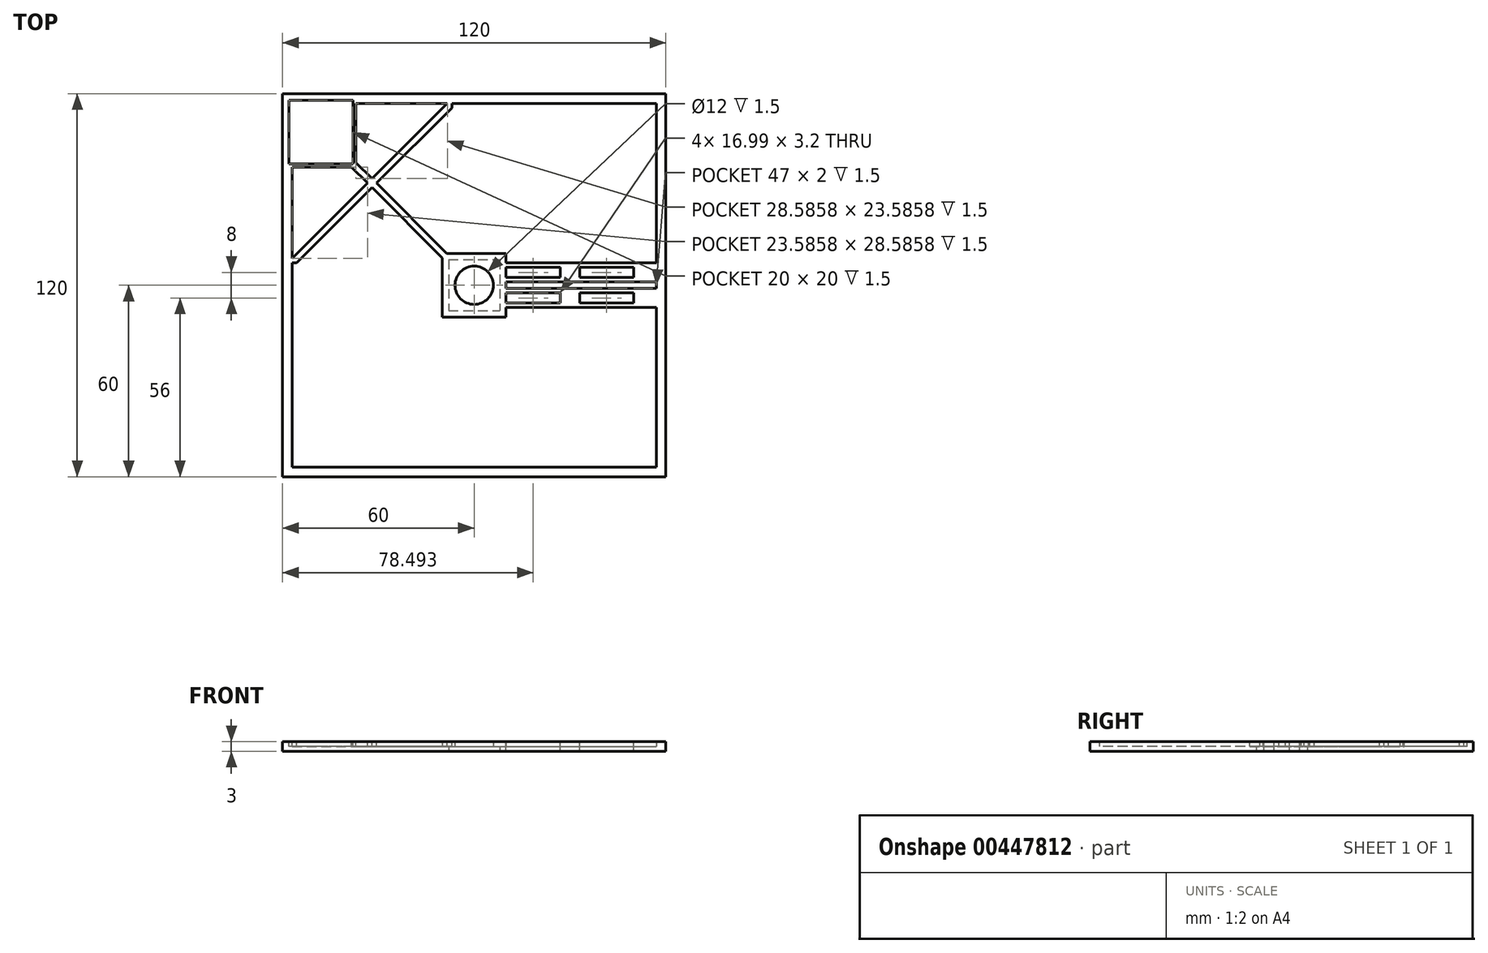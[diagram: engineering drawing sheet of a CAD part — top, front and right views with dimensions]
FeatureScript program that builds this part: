
annotation { "Feature Type Name" : "Feature", "Feature Type Description" : "" }
export const myFeature = defineFeature(function(context is Context, id is Id, definition is map)
    precondition{}
    {
        {
            var Q0;
            Q0=qCreatedBy(makeId("Top.planeOp"),FACE);
            var sketch = newSketch(context, id + "F0", { "sketchPlane" : qUnion([Q0])});
            skLineSegment(sketch, "E0.bottom", {"start": v(-60, 60) * mm, "end": v(60, 60) * mm});
            skLineSegment(sketch, "E0.top", {"start": v(-60, -60) * mm, "end": v(60, -60) * mm});
            skLineSegment(sketch, "E0.left", {"start": v(-60, 60) * mm, "end": v(-60, -60) * mm});
            skLineSegment(sketch, "E0.right", {"start": v(60, 60) * mm, "end": v(60, -60) * mm});
            skPoint(sketch, "E0.middle", {"position": v(0, 0) * mm});
            skSolve(sketch);
        }
        {
            var Q0;
            Q0 = qSketchRegion(id + "F0", true);
            extrude(context, id + "F1", {"entities" : qUnion([Q0]), "depth" : 3 * mm});
        }
        {
            var Q0;
            Q0=makeQuery(id+"F1.opExtrude","CAP_FACE",FACE,{"disambiguationData":[OSD([sQuery(id+"F0.wireOp",EDGE,"E0.bottom"),sQuery(id+"F0.wireOp",EDGE,"E0.top"),sQuery(id+"F0.wireOp",EDGE,"E0.left"),sQuery(id+"F0.wireOp",EDGE,"E0.right")])],"isStart":false});
            var sketch = newSketch(context, id + "F2", { "sketchPlane" : qUnion([Q0])});
            skLineSegment(sketch, "E1.bottom", {"start": v(-57, 57) * mm, "end": v(57, 57) * mm});
            skLineSegment(sketch, "E1.top", {"start": v(-57, -57) * mm, "end": v(57, -57) * mm});
            skLineSegment(sketch, "E1.left", {"start": v(-57, 57) * mm, "end": v(-57, -57) * mm});
            skLineSegment(sketch, "E1.right", {"start": v(57, 57) * mm, "end": v(57, -57) * mm});
            skPoint(sketch, "E1.middle", {"position": v(0, 0) * mm});
            skSolve(sketch);
        }
        {
            var Q0;
            Q0 = qSketchRegion(id + "F2", true);
            extrude(context, id + "F3", {"entities" : qUnion([Q0]), "operationType" : NewBodyOperationType.REMOVE, "oppositeDirection" : true, "depth" : 1.5 * mm});
        }
        {
            var Q0;
            Q0=makeQuery(id+"F3.boolean.opBoolean","COPY",FACE,{"derivedFrom":makeQuery(id+"F3.opExtrude","CAP_FACE",FACE,{"disambiguationData":[OSD([sQuery(id+"F2.wireOp",EDGE,"E1.bottom"),sQuery(id+"F2.wireOp",EDGE,"E1.top"),sQuery(id+"F2.wireOp",EDGE,"E1.left"),sQuery(id+"F2.wireOp",EDGE,"E1.right")])],"isStart":false})});
            var sketch = newSketch(context, id + "F4", { "sketchPlane" : qUnion([Q0])});
            skLineSegment(sketch, "E2", {"start": v(0, 0) * mm, "end": v(57, 0) * mm});
            skSolve(sketch);
        }
        {
            var Q0;
            {var subQ1=makeQuery(id+"F3.boolean.opBoolean","COPY",EDGE,{"derivedFrom":makeQuery(id+"F3.opExtrude","CAP_EDGE",EDGE,{"disambiguationData":[OSD([sQuery(id+"F2.wireOp",EDGE,"E1.bottom")])],"isStart":false})});Q0=makeQuery(id+"F4.imprint","IMPRINT",FACE,{"disambiguationData":[TD([[makeQuery(id+"F4.imprint","IMPRINT",EDGE,{"derivedFrom":subQ1}),-1.0]])]});}
            var sketch = newSketch(context, id + "F5", { "sketchPlane" : qUnion([Q0])});
            skLineSegment(sketch, "E3.bottom", {"start": v(-0.17, -1) * mm, "end": v(57, -1) * mm});
            skLineSegment(sketch, "E3.top", {"start": v(-0.17, -7) * mm, "end": v(57, -7) * mm});
            skLineSegment(sketch, "E3.left", {"start": v(-0.17, -1) * mm, "end": v(-0.17, -7) * mm});
            skLineSegment(sketch, "E3.right", {"start": v(57, -1) * mm, "end": v(57, -7) * mm});
            skLineSegment(sketch, "E4.MirrorCS", {"start": v(-0.17, 1) * mm, "end": v(57, 1) * mm});
            skLineSegment(sketch, "E5.MirrorCS", {"start": v(-0.17, 1) * mm, "end": v(-0.17, 7) * mm});
            skLineSegment(sketch, "E6.MirrorCS", {"start": v(-0.17, 7) * mm, "end": v(57, 7) * mm});
            skLineSegment(sketch, "E7.MirrorCS", {"start": v(57, 1) * mm, "end": v(57, 7) * mm});
            skSolve(sketch);
        }
        {
            var Q0;
            Q0 = qSketchRegion(id + "F5", true);
            extrude(context, id + "F6", {"entities" : qUnion([Q0]), "operationType" : NewBodyOperationType.ADD, "depth" : 1.5 * mm});
        }
        {
            var Q0;
            Q0=qCreatedBy(makeId("Front.planeOp"),FACE);
            var sketch = newSketch(context, id + "F7", { "sketchPlane" : qUnion([Q0])});
            skLineSegment(sketch, "E8", {"start": v(0, 0) * mm, "end": v(0, 23.02) * mm});
            skSolve(sketch);
        }
        {
            var Q0;
            {var subQ0=sQuery(id+"F5.wireOp",EDGE,"E7.MirrorCS");var subQ1=sQuery(id+"F5.wireOp",EDGE,"E6.MirrorCS");var subQ2=sQuery(id+"F5.wireOp",EDGE,"E5.MirrorCS");var subQ3=sQuery(id+"F5.wireOp",EDGE,"E4.MirrorCS");var subQ4=sQuery(id+"F5.wireOp",EDGE,"E3.right");var subQ5=sQuery(id+"F5.wireOp",EDGE,"E3.left");var subQ6=sQuery(id+"F5.wireOp",EDGE,"E3.top");var subQ7=sQuery(id+"F5.wireOp",EDGE,"E3.bottom");Q0=makeQuery(id+"FaZMyGU1LHLxgY4_1.3.F6.boolean.opBoolean","MERGE",FACE,{"derivedFrom":[makeQuery(id+"FaZMyGU1LHLxgY4_1.2.F6.boolean.opBoolean","MERGE",FACE,{"derivedFrom":[makeQuery(id+"FaZMyGU1LHLxgY4_1.1.F6.boolean.opBoolean","MERGE",FACE,{"derivedFrom":[makeQuery(id+"F6.boolean.opBoolean","MERGE",FACE,{"derivedFrom":[makeQuery(id+"F1.opExtrude","CAP_FACE",FACE,{"disambiguationData":[OSD([sQuery(id+"F0.wireOp",EDGE,"E0.bottom"),sQuery(id+"F0.wireOp",EDGE,"E0.top"),sQuery(id+"F0.wireOp",EDGE,"E0.left"),sQuery(id+"F0.wireOp",EDGE,"E0.right")])],"isStart":false}),makeQuery(id+"F6.opExtrude","CAP_FACE",FACE,{"disambiguationData":[OSD([subQ7,subQ6,subQ5,subQ4])],"isStart":false}),makeQuery(id+"F6.opExtrude","CAP_FACE",FACE,{"disambiguationData":[OSD([subQ3,subQ2,subQ1,subQ0])],"isStart":false})]}),makeQuery(id+"FaZMyGU1LHLxgY4_1.1.F6.opExtrude","CAP_FACE",FACE,{"disambiguationData":[OSD([subQ7,subQ6,subQ5,subQ4])],"isStart":false}),makeQuery(id+"FaZMyGU1LHLxgY4_1.1.F6.opExtrude","CAP_FACE",FACE,{"disambiguationData":[OSD([subQ3,subQ2,subQ1,subQ0])],"isStart":false})]}),makeQuery(id+"FaZMyGU1LHLxgY4_1.2.F6.opExtrude","CAP_FACE",FACE,{"disambiguationData":[OSD([subQ7,subQ6,subQ5,subQ4])],"isStart":false}),makeQuery(id+"FaZMyGU1LHLxgY4_1.2.F6.opExtrude","CAP_FACE",FACE,{"disambiguationData":[OSD([subQ3,subQ2,subQ1,subQ0])],"isStart":false})]}),makeQuery(id+"FaZMyGU1LHLxgY4_1.3.F6.opExtrude","CAP_FACE",FACE,{"disambiguationData":[OSD([subQ7,subQ6,subQ5,subQ4])],"isStart":false}),makeQuery(id+"FaZMyGU1LHLxgY4_1.3.F6.opExtrude","CAP_FACE",FACE,{"disambiguationData":[OSD([subQ3,subQ2,subQ1,subQ0])],"isStart":false})]});}
            var sketch = newSketch(context, id + "F8", { "sketchPlane" : qUnion([Q0])});
            skLineSegment(sketch, "E9.bottom", {"start": v(10, -5.6) * mm, "end": v(26.99, -5.6) * mm});
            skLineSegment(sketch, "E9.top", {"start": v(10, -2.4) * mm, "end": v(26.99, -2.4) * mm});
            skLineSegment(sketch, "E9.left", {"start": v(10, -5.6) * mm, "end": v(10, -2.4) * mm});
            skLineSegment(sketch, "E9.right", {"start": v(26.99, -5.6) * mm, "end": v(26.99, -2.4) * mm});
            skLineSegment(sketch, "E10.bottom", {"start": v(33, -5.6) * mm, "end": v(49.99, -5.6) * mm});
            skLineSegment(sketch, "E10.top", {"start": v(33, -2.4) * mm, "end": v(49.99, -2.4) * mm});
            skLineSegment(sketch, "E10.left", {"start": v(33, -5.6) * mm, "end": v(33, -2.4) * mm});
            skLineSegment(sketch, "E10.right", {"start": v(49.99, -5.6) * mm, "end": v(49.99, -2.4) * mm});
            skLineSegment(sketch, "E11.MirrorCS", {"start": v(49.99, 5.6) * mm, "end": v(49.99, 2.4) * mm});
            skLineSegment(sketch, "E12.MirrorCS", {"start": v(26.99, 5.6) * mm, "end": v(26.99, 2.4) * mm});
            skLineSegment(sketch, "E13.MirrorCS", {"start": v(10, 5.6) * mm, "end": v(10, 2.4) * mm});
            skLineSegment(sketch, "E14.MirrorCS", {"start": v(10, 2.4) * mm, "end": v(26.99, 2.4) * mm});
            skLineSegment(sketch, "E15.MirrorCS", {"start": v(10, 5.6) * mm, "end": v(26.99, 5.6) * mm});
            skLineSegment(sketch, "E16.MirrorCS", {"start": v(33, 5.6) * mm, "end": v(49.99, 5.6) * mm});
            skLineSegment(sketch, "E17.MirrorCS", {"start": v(33, 2.4) * mm, "end": v(49.99, 2.4) * mm});
            skLineSegment(sketch, "E18.MirrorCS", {"start": v(33, 5.6) * mm, "end": v(33, 2.4) * mm});
            skSolve(sketch);
        }
        {
            var Q0;
            Q0 = qSketchRegion(id + "F8", true);
            extrude(context, id + "F9", {"entities" : qUnion([Q0]), "operationType" : NewBodyOperationType.REMOVE, "oppositeDirection" : true, "depth" : 3 * mm});
        }
        {
            var Q0;
            {var subQ1=makeQuery(id+"F3.boolean.opBoolean","COPY",EDGE,{"derivedFrom":makeQuery(id+"F3.opExtrude","CAP_EDGE",EDGE,{"disambiguationData":[OSD([sQuery(id+"F2.wireOp",EDGE,"E1.bottom")])],"isStart":false})});Q0=makeQuery(id+"F4.imprint","IMPRINT",FACE,{"disambiguationData":[TD([[makeQuery(id+"F4.imprint","IMPRINT",EDGE,{"derivedFrom":subQ1}),-1.0]])]});}
            var sketch = newSketch(context, id + "F10", { "sketchPlane" : qUnion([Q0])});
            skLineSegment(sketch, "E19.bottom", {"start": v(-59, 59) * mm, "end": v(-37, 59) * mm});
            skLineSegment(sketch, "E19.top", {"start": v(-59, 37) * mm, "end": v(-37, 37) * mm});
            skLineSegment(sketch, "E19.left", {"start": v(-59, 59) * mm, "end": v(-59, 37) * mm});
            skLineSegment(sketch, "E19.right", {"start": v(-37, 59) * mm, "end": v(-37, 37) * mm});
            skPoint(sketch, "E19.middle", {"position": v(-48, 48) * mm});
            skLineSegment(sketch, "E20.bottom", {"start": v(-40.5, 55.5) * mm, "end": v(-55.5, 55.5) * mm});
            skLineSegment(sketch, "E20.top", {"start": v(-40.5, 40.5) * mm, "end": v(-55.5, 40.5) * mm});
            skLineSegment(sketch, "E20.left", {"start": v(-40.5, 55.5) * mm, "end": v(-40.5, 40.5) * mm});
            skLineSegment(sketch, "E20.right", {"start": v(-55.5, 55.5) * mm, "end": v(-55.5, 40.5) * mm});
            skSolve(sketch);
        }
        {
            var Q0;
            Q0 = qSketchRegion(id + "F10", true);
            extrude(context, id + "F11", {"entities" : qUnion([Q0]), "operationType" : NewBodyOperationType.ADD, "depth" : 1.5 * mm});
        }
        {
            var Q0;
            {var subQ0=sQuery(id+"F10.wireOp",EDGE,"E20.right");var subQ1=sQuery(id+"F10.wireOp",EDGE,"E20.left");var subQ2=sQuery(id+"F10.wireOp",EDGE,"E20.top");var subQ3=sQuery(id+"F10.wireOp",EDGE,"E20.bottom");var subQ4=sQuery(id+"F10.wireOp",EDGE,"E19.right");var subQ5=sQuery(id+"F10.wireOp",EDGE,"E19.left");var subQ6=sQuery(id+"F10.wireOp",EDGE,"E19.top");var subQ7=sQuery(id+"F10.wireOp",EDGE,"E19.bottom");var subQ8=sQuery(id+"F5.wireOp",EDGE,"E7.MirrorCS");var subQ9=sQuery(id+"F5.wireOp",EDGE,"E6.MirrorCS");var subQ10=sQuery(id+"F5.wireOp",EDGE,"E5.MirrorCS");var subQ11=sQuery(id+"F5.wireOp",EDGE,"E4.MirrorCS");var subQ12=sQuery(id+"F5.wireOp",EDGE,"E3.right");var subQ13=sQuery(id+"F5.wireOp",EDGE,"E3.left");var subQ14=sQuery(id+"F5.wireOp",EDGE,"E3.top");var subQ15=sQuery(id+"F5.wireOp",EDGE,"E3.bottom");Q0=makeQuery(id+"F5DrHdDq57b8UHH_1.3.F11.boolean.opBoolean","MERGE",FACE,{"derivedFrom":[makeQuery(id+"F5DrHdDq57b8UHH_1.2.F11.boolean.opBoolean","MERGE",FACE,{"derivedFrom":[makeQuery(id+"F5DrHdDq57b8UHH_1.1.F11.boolean.opBoolean","MERGE",FACE,{"derivedFrom":[makeQuery(id+"F11.boolean.opBoolean","MERGE",FACE,{"derivedFrom":[makeQuery(id+"FaZMyGU1LHLxgY4_1.3.F6.boolean.opBoolean","MERGE",FACE,{"derivedFrom":[makeQuery(id+"FaZMyGU1LHLxgY4_1.2.F6.boolean.opBoolean","MERGE",FACE,{"derivedFrom":[makeQuery(id+"FaZMyGU1LHLxgY4_1.1.F6.boolean.opBoolean","MERGE",FACE,{"derivedFrom":[makeQuery(id+"F6.boolean.opBoolean","MERGE",FACE,{"derivedFrom":[makeQuery(id+"F1.opExtrude","CAP_FACE",FACE,{"disambiguationData":[OSD([sQuery(id+"F0.wireOp",EDGE,"E0.bottom"),sQuery(id+"F0.wireOp",EDGE,"E0.top"),sQuery(id+"F0.wireOp",EDGE,"E0.left"),sQuery(id+"F0.wireOp",EDGE,"E0.right")])],"isStart":false}),makeQuery(id+"F6.opExtrude","CAP_FACE",FACE,{"disambiguationData":[OSD([subQ15,subQ14,subQ13,subQ12])],"isStart":false}),makeQuery(id+"F6.opExtrude","CAP_FACE",FACE,{"disambiguationData":[OSD([subQ11,subQ10,subQ9,subQ8])],"isStart":false})]}),makeQuery(id+"FaZMyGU1LHLxgY4_1.1.F6.opExtrude","CAP_FACE",FACE,{"disambiguationData":[OSD([subQ15,subQ14,subQ13,subQ12])],"isStart":false}),makeQuery(id+"FaZMyGU1LHLxgY4_1.1.F6.opExtrude","CAP_FACE",FACE,{"disambiguationData":[OSD([subQ11,subQ10,subQ9,subQ8])],"isStart":false})]}),makeQuery(id+"FaZMyGU1LHLxgY4_1.2.F6.opExtrude","CAP_FACE",FACE,{"disambiguationData":[OSD([subQ15,subQ14,subQ13,subQ12])],"isStart":false}),makeQuery(id+"FaZMyGU1LHLxgY4_1.2.F6.opExtrude","CAP_FACE",FACE,{"disambiguationData":[OSD([subQ11,subQ10,subQ9,subQ8])],"isStart":false})]}),makeQuery(id+"FaZMyGU1LHLxgY4_1.3.F6.opExtrude","CAP_FACE",FACE,{"disambiguationData":[OSD([subQ15,subQ14,subQ13,subQ12])],"isStart":false}),makeQuery(id+"FaZMyGU1LHLxgY4_1.3.F6.opExtrude","CAP_FACE",FACE,{"disambiguationData":[OSD([subQ11,subQ10,subQ9,subQ8])],"isStart":false})]}),makeQuery(id+"F11.opExtrude","CAP_FACE",FACE,{"disambiguationData":[OSD([subQ7,subQ6,subQ5,subQ4,subQ3,subQ2,subQ1,subQ0])],"isStart":false})]}),makeQuery(id+"F5DrHdDq57b8UHH_1.1.F11.opExtrude","CAP_FACE",FACE,{"disambiguationData":[OSD([subQ7,subQ6,subQ5,subQ4,subQ3,subQ2,subQ1,subQ0])],"isStart":false})]}),makeQuery(id+"F5DrHdDq57b8UHH_1.2.F11.opExtrude","CAP_FACE",FACE,{"disambiguationData":[OSD([subQ7,subQ6,subQ5,subQ4,subQ3,subQ2,subQ1,subQ0])],"isStart":false})]}),makeQuery(id+"F5DrHdDq57b8UHH_1.3.F11.opExtrude","CAP_FACE",FACE,{"disambiguationData":[OSD([subQ7,subQ6,subQ5,subQ4,subQ3,subQ2,subQ1,subQ0])],"isStart":false})]});}
            var sketch = newSketch(context, id + "F12", { "sketchPlane" : qUnion([Q0])});
            skLineSegment(sketch, "E21.bottom", {"start": v(-38, 58) * mm, "end": v(-58, 58) * mm});
            skLineSegment(sketch, "E21.top", {"start": v(-38, 38) * mm, "end": v(-58, 38) * mm});
            skLineSegment(sketch, "E21.left", {"start": v(-38, 58) * mm, "end": v(-38, 38) * mm});
            skLineSegment(sketch, "E21.right", {"start": v(-58, 58) * mm, "end": v(-58, 38) * mm});
            skPoint(sketch, "E21.middle", {"position": v(-48, 48) * mm});
            skLineSegment(sketch, "E22.bottom", {"start": v(-41, 55) * mm, "end": v(-55, 55) * mm});
            skLineSegment(sketch, "E22.top", {"start": v(-41, 41) * mm, "end": v(-55, 41) * mm});
            skLineSegment(sketch, "E22.left", {"start": v(-41, 55) * mm, "end": v(-41, 41) * mm});
            skLineSegment(sketch, "E22.right", {"start": v(-55, 55) * mm, "end": v(-55, 41) * mm});
            skSolve(sketch);
        }
        {
            var Q0;
            Q0 = qSketchRegion(id + "F12", true);
            extrude(context, id + "F13", {"entities" : qUnion([Q0]), "operationType" : NewBodyOperationType.REMOVE, "oppositeDirection" : true, "depth" : 1.5 * mm});
        }
        {
            var Q0;
            {var subQ0=sQuery(id+"F10.wireOp",EDGE,"E19.top");var subQ2=sQuery(id+"F10.wireOp",EDGE,"E19.right");var subQ65=sQuery(id+"F5.wireOp",EDGE,"E3.top");var subQ67=sQuery(id+"F5.wireOp",EDGE,"E4.MirrorCS");var subQ69=sQuery(id+"F5.wireOp",EDGE,"E3.bottom");var subQ74=sQuery(id+"F5.wireOp",EDGE,"E6.MirrorCS");var subQ81=sQuery(id+"F0.wireOp",EDGE,"E0.bottom");var subQ82=makeQuery(id+"F1.opExtrude","SWEPT_FACE",FACE,{"disambiguationData":[OSD([subQ81])]});var subQ86=sQuery(id+"F0.wireOp",EDGE,"E0.left");var subQ91=sQuery(id+"F0.wireOp",EDGE,"E0.top");var subQ110=sQuery(id+"F0.wireOp",EDGE,"E0.right");var subQ146=sQuery(id+"F10.wireOp",EDGE,"E20.top");var subQ148=sQuery(id+"F10.wireOp",EDGE,"E20.bottom");var subQ150=sQuery(id+"F10.wireOp",EDGE,"E20.left");var subQ152=sQuery(id+"F10.wireOp",EDGE,"E20.right");var subQ158=sQuery(id+"F10.wireOp",EDGE,"E19.left");var subQ159=sQuery(id+"F10.wireOp",EDGE,"E19.bottom");var subQ160=sQuery(id+"F5.wireOp",EDGE,"E7.MirrorCS");var subQ161=sQuery(id+"F5.wireOp",EDGE,"E5.MirrorCS");var subQ162=sQuery(id+"F5.wireOp",EDGE,"E3.right");var subQ163=sQuery(id+"F5.wireOp",EDGE,"E3.left");Q0=makeQuery(id+"FvlwYFeN0eFixSL_1.3.F13.boolean.opBoolean","SPLIT",FACE,{"disambiguationData":[TD([subQ82])],"derivedFrom":makeQuery(id+"FvlwYFeN0eFixSL_1.2.F13.boolean.opBoolean","SPLIT",FACE,{"disambiguationData":[TD([subQ82])],"derivedFrom":makeQuery(id+"FvlwYFeN0eFixSL_1.1.F13.boolean.opBoolean","SPLIT",FACE,{"disambiguationData":[TD([subQ82])],"derivedFrom":makeQuery(id+"F13.boolean.opBoolean","SPLIT",FACE,{"disambiguationData":[TD([subQ82])],"derivedFrom":makeQuery(id+"F5DrHdDq57b8UHH_1.3.F11.boolean.opBoolean","MERGE",FACE,{"derivedFrom":[makeQuery(id+"F5DrHdDq57b8UHH_1.2.F11.boolean.opBoolean","MERGE",FACE,{"derivedFrom":[makeQuery(id+"F5DrHdDq57b8UHH_1.1.F11.boolean.opBoolean","MERGE",FACE,{"derivedFrom":[makeQuery(id+"F11.boolean.opBoolean","MERGE",FACE,{"derivedFrom":[makeQuery(id+"FaZMyGU1LHLxgY4_1.3.F6.boolean.opBoolean","MERGE",FACE,{"derivedFrom":[makeQuery(id+"FaZMyGU1LHLxgY4_1.2.F6.boolean.opBoolean","MERGE",FACE,{"derivedFrom":[makeQuery(id+"FaZMyGU1LHLxgY4_1.1.F6.boolean.opBoolean","MERGE",FACE,{"derivedFrom":[makeQuery(id+"F6.boolean.opBoolean","MERGE",FACE,{"derivedFrom":[makeQuery(id+"F1.opExtrude","CAP_FACE",FACE,{"disambiguationData":[OSD([subQ81,subQ91,subQ86,subQ110])],"isStart":false}),makeQuery(id+"F6.opExtrude","CAP_FACE",FACE,{"disambiguationData":[OSD([subQ69,subQ65,subQ163,subQ162])],"isStart":false}),makeQuery(id+"F6.opExtrude","CAP_FACE",FACE,{"disambiguationData":[OSD([subQ67,subQ161,subQ74,subQ160])],"isStart":false})]}),makeQuery(id+"FaZMyGU1LHLxgY4_1.1.F6.opExtrude","CAP_FACE",FACE,{"disambiguationData":[OSD([subQ69,subQ65,subQ163,subQ162])],"isStart":false}),makeQuery(id+"FaZMyGU1LHLxgY4_1.1.F6.opExtrude","CAP_FACE",FACE,{"disambiguationData":[OSD([subQ67,subQ161,subQ74,subQ160])],"isStart":false})]}),makeQuery(id+"FaZMyGU1LHLxgY4_1.2.F6.opExtrude","CAP_FACE",FACE,{"disambiguationData":[OSD([subQ69,subQ65,subQ163,subQ162])],"isStart":false}),makeQuery(id+"FaZMyGU1LHLxgY4_1.2.F6.opExtrude","CAP_FACE",FACE,{"disambiguationData":[OSD([subQ67,subQ161,subQ74,subQ160])],"isStart":false})]}),makeQuery(id+"FaZMyGU1LHLxgY4_1.3.F6.opExtrude","CAP_FACE",FACE,{"disambiguationData":[OSD([subQ69,subQ65,subQ163,subQ162])],"isStart":false}),makeQuery(id+"FaZMyGU1LHLxgY4_1.3.F6.opExtrude","CAP_FACE",FACE,{"disambiguationData":[OSD([subQ67,subQ161,subQ74,subQ160])],"isStart":false})]}),makeQuery(id+"F11.opExtrude","CAP_FACE",FACE,{"disambiguationData":[OSD([subQ159,subQ0,subQ158,subQ2,subQ148,subQ146,subQ150,subQ152])],"isStart":false})]}),makeQuery(id+"F5DrHdDq57b8UHH_1.1.F11.opExtrude","CAP_FACE",FACE,{"disambiguationData":[OSD([subQ159,subQ0,subQ158,subQ2,subQ148,subQ146,subQ150,subQ152])],"isStart":false})]}),makeQuery(id+"F5DrHdDq57b8UHH_1.2.F11.opExtrude","CAP_FACE",FACE,{"disambiguationData":[OSD([subQ159,subQ0,subQ158,subQ2,subQ148,subQ146,subQ150,subQ152])],"isStart":false})]}),makeQuery(id+"F5DrHdDq57b8UHH_1.3.F11.opExtrude","CAP_FACE",FACE,{"disambiguationData":[OSD([subQ159,subQ0,subQ158,subQ2,subQ148,subQ146,subQ150,subQ152])],"isStart":false})]})})})})});}
            var sketch = newSketch(context, id + "F14", { "sketchPlane" : qUnion([Q0])});
            skLineSegment(sketch, "E23", {"start": v(-7, 57) * mm, "end": v(-57, 7) * mm});
            skLineSegment(sketch, "E24", {"start": v(-37, 37) * mm, "end": v(-7, 7) * mm});
            skSolve(sketch);
        }
        {
            var Q0;
            {var subQ14=sQuery(id+"F0.wireOp",EDGE,"E0.bottom");Q0=makeQuery(id+"F14.imprint","IMPRINT",FACE,{"disambiguationData":[TD([[makeQuery(id+"F14.imprint","IMPRINT",EDGE,{"derivedFrom":makeQuery(id+"F1.opExtrude","CAP_EDGE",EDGE,{"disambiguationData":[OSD([subQ14])],"isStart":false})}),-1.0]])]});}
            var sketch = newSketch(context, id + "F15", { "sketchPlane" : qUnion([Q0])});
            skLineSegment(sketch, "E25", {"start": v(-7, 8.41) * mm, "end": v(-37, 38.41) * mm});
            skLineSegment(sketch, "E26", {"start": v(-37, 38.41) * mm, "end": v(-37, 37) * mm});
            skLineSegment(sketch, "E27", {"start": v(-7, 8.41) * mm, "end": v(-7, 7) * mm});
            skLineSegment(sketch, "E28.MirrorCS", {"start": v(-38.41, 37) * mm, "end": v(-37, 37) * mm});
            skLineSegment(sketch, "E29.MirrorCS", {"start": v(-8.41, 7) * mm, "end": v(-38.41, 37) * mm});
            skLineSegment(sketch, "E30.MirrorCS", {"start": v(-8.41, 7) * mm, "end": v(-7, 7) * mm});
            skSolve(sketch);
        }
        {
            var Q0;
            Q0 = qSketchRegion(id + "F15", true);
            extrude(context, id + "F16", {"entities" : qUnion([Q0]), "operationType" : NewBodyOperationType.ADD, "oppositeDirection" : true, "depth" : 1.5 * mm});
        }
        {
            var Q0;
            {var subQ14=sQuery(id+"F0.wireOp",EDGE,"E0.bottom");Q0=makeQuery(id+"F14.imprint","IMPRINT",FACE,{"disambiguationData":[TD([[makeQuery(id+"F14.imprint","IMPRINT",EDGE,{"derivedFrom":makeQuery(id+"F1.opExtrude","CAP_EDGE",EDGE,{"disambiguationData":[OSD([subQ14])],"isStart":false})}),-1.0]])]});}
            var sketch = newSketch(context, id + "F17", { "sketchPlane" : qUnion([Q0])});
            skLineSegment(sketch, "E31", {"start": v(-7, 57) * mm, "end": v(-7, 55.59) * mm});
            skLineSegment(sketch, "E32", {"start": v(-7, 55.59) * mm, "end": v(-55.59, 7) * mm});
            skLineSegment(sketch, "E33", {"start": v(-55.59, 7) * mm, "end": v(-57, 7) * mm});
            skLineSegment(sketch, "E34.MirrorCS", {"start": v(-7, 57) * mm, "end": v(-8.41, 57) * mm});
            skLineSegment(sketch, "E35.MirrorCS", {"start": v(-8.41, 57) * mm, "end": v(-57, 8.41) * mm});
            skLineSegment(sketch, "E36.MirrorCS", {"start": v(-57, 8.41) * mm, "end": v(-57, 7) * mm});
            skSolve(sketch);
        }
        {
            var Q0;
            Q0 = qSketchRegion(id + "F17", true);
            extrude(context, id + "F18", {"entities" : qUnion([Q0]), "operationType" : NewBodyOperationType.ADD, "oppositeDirection" : true, "depth" : 1.5 * mm});
        }
        {
            var Q0;
            {var subQ0=sQuery(id+"F17.wireOp",EDGE,"E36.MirrorCS");var subQ1=sQuery(id+"F17.wireOp",EDGE,"E35.MirrorCS");var subQ2=sQuery(id+"F17.wireOp",EDGE,"E34.MirrorCS");var subQ3=sQuery(id+"F17.wireOp",EDGE,"E33");var subQ4=sQuery(id+"F17.wireOp",EDGE,"E32");var subQ5=sQuery(id+"F17.wireOp",EDGE,"E31");var subQ6=sQuery(id+"F15.wireOp",EDGE,"E30.MirrorCS");var subQ7=sQuery(id+"F15.wireOp",EDGE,"E29.MirrorCS");var subQ8=sQuery(id+"F15.wireOp",EDGE,"E28.MirrorCS");var subQ9=sQuery(id+"F15.wireOp",EDGE,"E27");var subQ10=sQuery(id+"F15.wireOp",EDGE,"E26");var subQ11=sQuery(id+"F15.wireOp",EDGE,"E25");var subQ12=sQuery(id+"F10.wireOp",EDGE,"E19.top");var subQ14=sQuery(id+"F10.wireOp",EDGE,"E19.right");var subQ77=sQuery(id+"F5.wireOp",EDGE,"E3.top");var subQ79=sQuery(id+"F5.wireOp",EDGE,"E4.MirrorCS");var subQ81=sQuery(id+"F5.wireOp",EDGE,"E3.bottom");var subQ86=sQuery(id+"F5.wireOp",EDGE,"E6.MirrorCS");var subQ93=sQuery(id+"F0.wireOp",EDGE,"E0.bottom");var subQ94=makeQuery(id+"F1.opExtrude","SWEPT_FACE",FACE,{"disambiguationData":[OSD([subQ93])]});var subQ98=sQuery(id+"F0.wireOp",EDGE,"E0.left");var subQ103=sQuery(id+"F0.wireOp",EDGE,"E0.top");var subQ122=sQuery(id+"F0.wireOp",EDGE,"E0.right");var subQ158=sQuery(id+"F10.wireOp",EDGE,"E20.top");var subQ160=sQuery(id+"F10.wireOp",EDGE,"E20.bottom");var subQ162=sQuery(id+"F10.wireOp",EDGE,"E20.left");var subQ164=sQuery(id+"F10.wireOp",EDGE,"E20.right");var subQ170=sQuery(id+"F10.wireOp",EDGE,"E19.left");var subQ171=sQuery(id+"F10.wireOp",EDGE,"E19.bottom");var subQ172=sQuery(id+"F5.wireOp",EDGE,"E7.MirrorCS");var subQ173=sQuery(id+"F5.wireOp",EDGE,"E5.MirrorCS");var subQ174=sQuery(id+"F5.wireOp",EDGE,"E3.right");var subQ175=sQuery(id+"F5.wireOp",EDGE,"E3.left");Q0=makeQuery(id+"FomB0YtQIJf065d_1.3.F18.boolean.opBoolean","MERGE",FACE,{"derivedFrom":[makeQuery(id+"FomB0YtQIJf065d_1.2.F18.boolean.opBoolean","MERGE",FACE,{"derivedFrom":[makeQuery(id+"FomB0YtQIJf065d_1.1.F18.boolean.opBoolean","MERGE",FACE,{"derivedFrom":[makeQuery(id+"F18.boolean.opBoolean","MERGE",FACE,{"derivedFrom":[makeQuery(id+"FP1tWfbVCGLyuFH_1.3.F16.boolean.opBoolean","MERGE",FACE,{"derivedFrom":[makeQuery(id+"FP1tWfbVCGLyuFH_1.2.F16.boolean.opBoolean","MERGE",FACE,{"derivedFrom":[makeQuery(id+"FP1tWfbVCGLyuFH_1.1.F16.boolean.opBoolean","MERGE",FACE,{"derivedFrom":[makeQuery(id+"F16.boolean.opBoolean","MERGE",FACE,{"derivedFrom":[makeQuery(id+"FvlwYFeN0eFixSL_1.3.F13.boolean.opBoolean","SPLIT",FACE,{"disambiguationData":[TD([subQ94])],"derivedFrom":makeQuery(id+"FvlwYFeN0eFixSL_1.2.F13.boolean.opBoolean","SPLIT",FACE,{"disambiguationData":[TD([subQ94])],"derivedFrom":makeQuery(id+"FvlwYFeN0eFixSL_1.1.F13.boolean.opBoolean","SPLIT",FACE,{"disambiguationData":[TD([subQ94])],"derivedFrom":makeQuery(id+"F13.boolean.opBoolean","SPLIT",FACE,{"disambiguationData":[TD([subQ94])],"derivedFrom":makeQuery(id+"F5DrHdDq57b8UHH_1.3.F11.boolean.opBoolean","MERGE",FACE,{"derivedFrom":[makeQuery(id+"F5DrHdDq57b8UHH_1.2.F11.boolean.opBoolean","MERGE",FACE,{"derivedFrom":[makeQuery(id+"F5DrHdDq57b8UHH_1.1.F11.boolean.opBoolean","MERGE",FACE,{"derivedFrom":[makeQuery(id+"F11.boolean.opBoolean","MERGE",FACE,{"derivedFrom":[makeQuery(id+"FaZMyGU1LHLxgY4_1.3.F6.boolean.opBoolean","MERGE",FACE,{"derivedFrom":[makeQuery(id+"FaZMyGU1LHLxgY4_1.2.F6.boolean.opBoolean","MERGE",FACE,{"derivedFrom":[makeQuery(id+"FaZMyGU1LHLxgY4_1.1.F6.boolean.opBoolean","MERGE",FACE,{"derivedFrom":[makeQuery(id+"F6.boolean.opBoolean","MERGE",FACE,{"derivedFrom":[makeQuery(id+"F1.opExtrude","CAP_FACE",FACE,{"disambiguationData":[OSD([subQ93,subQ103,subQ98,subQ122])],"isStart":false}),makeQuery(id+"F6.opExtrude","CAP_FACE",FACE,{"disambiguationData":[OSD([subQ81,subQ77,subQ175,subQ174])],"isStart":false}),makeQuery(id+"F6.opExtrude","CAP_FACE",FACE,{"disambiguationData":[OSD([subQ79,subQ173,subQ86,subQ172])],"isStart":false})]}),makeQuery(id+"FaZMyGU1LHLxgY4_1.1.F6.opExtrude","CAP_FACE",FACE,{"disambiguationData":[OSD([subQ81,subQ77,subQ175,subQ174])],"isStart":false}),makeQuery(id+"FaZMyGU1LHLxgY4_1.1.F6.opExtrude","CAP_FACE",FACE,{"disambiguationData":[OSD([subQ79,subQ173,subQ86,subQ172])],"isStart":false})]}),makeQuery(id+"FaZMyGU1LHLxgY4_1.2.F6.opExtrude","CAP_FACE",FACE,{"disambiguationData":[OSD([subQ81,subQ77,subQ175,subQ174])],"isStart":false}),makeQuery(id+"FaZMyGU1LHLxgY4_1.2.F6.opExtrude","CAP_FACE",FACE,{"disambiguationData":[OSD([subQ79,subQ173,subQ86,subQ172])],"isStart":false})]}),makeQuery(id+"FaZMyGU1LHLxgY4_1.3.F6.opExtrude","CAP_FACE",FACE,{"disambiguationData":[OSD([subQ81,subQ77,subQ175,subQ174])],"isStart":false}),makeQuery(id+"FaZMyGU1LHLxgY4_1.3.F6.opExtrude","CAP_FACE",FACE,{"disambiguationData":[OSD([subQ79,subQ173,subQ86,subQ172])],"isStart":false})]}),makeQuery(id+"F11.opExtrude","CAP_FACE",FACE,{"disambiguationData":[OSD([subQ171,subQ12,subQ170,subQ14,subQ160,subQ158,subQ162,subQ164])],"isStart":false})]}),makeQuery(id+"F5DrHdDq57b8UHH_1.1.F11.opExtrude","CAP_FACE",FACE,{"disambiguationData":[OSD([subQ171,subQ12,subQ170,subQ14,subQ160,subQ158,subQ162,subQ164])],"isStart":false})]}),makeQuery(id+"F5DrHdDq57b8UHH_1.2.F11.opExtrude","CAP_FACE",FACE,{"disambiguationData":[OSD([subQ171,subQ12,subQ170,subQ14,subQ160,subQ158,subQ162,subQ164])],"isStart":false})]}),makeQuery(id+"F5DrHdDq57b8UHH_1.3.F11.opExtrude","CAP_FACE",FACE,{"disambiguationData":[OSD([subQ171,subQ12,subQ170,subQ14,subQ160,subQ158,subQ162,subQ164])],"isStart":false})]})})})})}),makeQuery(id+"F16.opExtrude","CAP_FACE",FACE,{"disambiguationData":[OSD([subQ11,subQ10,subQ9,subQ8,subQ7,subQ6])],"isStart":true})]}),makeQuery(id+"FP1tWfbVCGLyuFH_1.1.F16.opExtrude","CAP_FACE",FACE,{"disambiguationData":[OSD([subQ11,subQ10,subQ9,subQ8,subQ7,subQ6])],"isStart":true})]}),makeQuery(id+"FP1tWfbVCGLyuFH_1.2.F16.opExtrude","CAP_FACE",FACE,{"disambiguationData":[OSD([subQ11,subQ10,subQ9,subQ8,subQ7,subQ6])],"isStart":true})]}),makeQuery(id+"FP1tWfbVCGLyuFH_1.3.F16.opExtrude","CAP_FACE",FACE,{"disambiguationData":[OSD([subQ11,subQ10,subQ9,subQ8,subQ7,subQ6])],"isStart":true})]}),makeQuery(id+"F18.opExtrude","CAP_FACE",FACE,{"disambiguationData":[OSD([subQ5,subQ4,subQ3,subQ2,subQ1,subQ0])],"isStart":true})]}),makeQuery(id+"FomB0YtQIJf065d_1.1.F18.opExtrude","CAP_FACE",FACE,{"disambiguationData":[OSD([subQ5,subQ4,subQ3,subQ2,subQ1,subQ0])],"isStart":true})]}),makeQuery(id+"FomB0YtQIJf065d_1.2.F18.opExtrude","CAP_FACE",FACE,{"disambiguationData":[OSD([subQ5,subQ4,subQ3,subQ2,subQ1,subQ0])],"isStart":true})]}),makeQuery(id+"FomB0YtQIJf065d_1.3.F18.opExtrude","CAP_FACE",FACE,{"disambiguationData":[OSD([subQ5,subQ4,subQ3,subQ2,subQ1,subQ0])],"isStart":true})]});}
            var sketch = newSketch(context, id + "F19", { "sketchPlane" : qUnion([Q0])});
            skLineSegment(sketch, "E37.bottom", {"start": v(-10, -10) * mm, "end": v(10, -10) * mm});
            skLineSegment(sketch, "E37.top", {"start": v(-10, 10) * mm, "end": v(10, 10) * mm});
            skLineSegment(sketch, "E37.left", {"start": v(-10, -10) * mm, "end": v(-10, 10) * mm});
            skLineSegment(sketch, "E37.right", {"start": v(10, -10) * mm, "end": v(10, 10) * mm});
            skPoint(sketch, "E37.middle", {"position": v(0, 0) * mm});
            skSolve(sketch);
        }
        {
            var Q0;
            Q0 = qSketchRegion(id + "F19", true);
            extrude(context, id + "F20", {"entities" : qUnion([Q0]), "operationType" : NewBodyOperationType.ADD, "oppositeDirection" : true, "depth" : 1.5 * mm});
        }
        {
            var Q0;
            Q0=makeQuery(id+"F1.opExtrude","CAP_FACE",FACE,{"disambiguationData":[OSD([sQuery(id+"F0.wireOp",EDGE,"E0.bottom"),sQuery(id+"F0.wireOp",EDGE,"E0.top"),sQuery(id+"F0.wireOp",EDGE,"E0.left"),sQuery(id+"F0.wireOp",EDGE,"E0.right")])],"isStart":true});
            var sketch = newSketch(context, id + "F21", { "sketchPlane" : qUnion([Q0])});
            skCircle(sketch, "E38", {"center": v(0, 0) * mm, "radius": 6 * mm});
            skSolve(sketch);
        }
        {
            var Q0;
            Q0 = qSketchRegion(id + "F21", true);
            extrude(context, id + "F22", {"entities" : qUnion([Q0]), "operationType" : NewBodyOperationType.REMOVE, "oppositeDirection" : true, "depth" : 3 * mm});
        }
        {
            var Q0;
            Q0=makeQuery(id+"F1.opExtrude","CAP_FACE",FACE,{"disambiguationData":[OSD([sQuery(id+"F0.wireOp",EDGE,"E0.bottom"),sQuery(id+"F0.wireOp",EDGE,"E0.top"),sQuery(id+"F0.wireOp",EDGE,"E0.left"),sQuery(id+"F0.wireOp",EDGE,"E0.right")])],"isStart":true});
            var sketch = newSketch(context, id + "F23", { "sketchPlane" : qUnion([Q0])});
            skLineSegment(sketch, "E39.bottom", {"start": v(-8, -8) * mm, "end": v(8, -8) * mm});
            skLineSegment(sketch, "E39.top", {"start": v(-8, 8) * mm, "end": v(8, 8) * mm});
            skLineSegment(sketch, "E39.left", {"start": v(-8, -8) * mm, "end": v(-8, 8) * mm});
            skLineSegment(sketch, "E39.right", {"start": v(8, -8) * mm, "end": v(8, 8) * mm});
            skPoint(sketch, "E39.middle", {"position": v(0, 0) * mm});
            skSolve(sketch);
        }
        {
            var Q0;
            Q0 = qSketchRegion(id + "F23", true);
            extrude(context, id + "F24", {"entities" : qUnion([Q0]), "operationType" : NewBodyOperationType.REMOVE, "oppositeDirection" : true, "depth" : 1.5 * mm});
        }
    });
